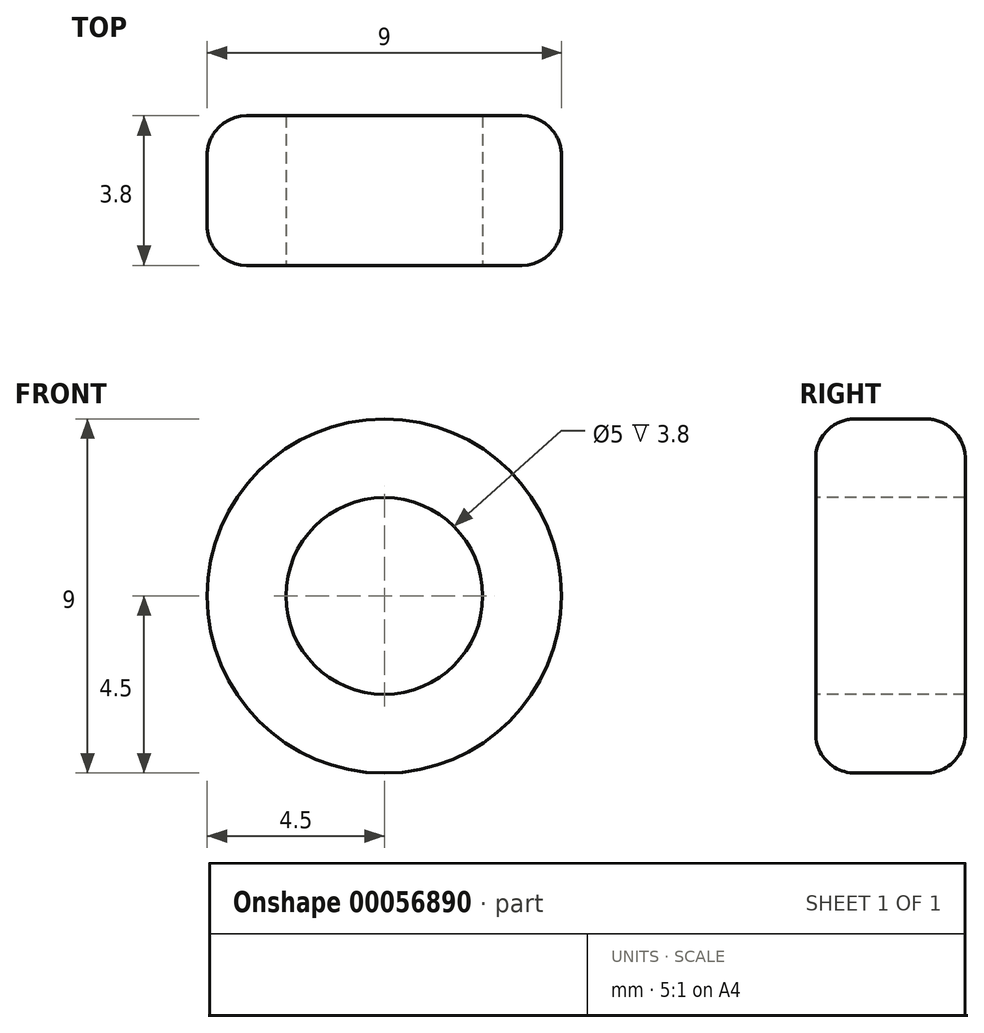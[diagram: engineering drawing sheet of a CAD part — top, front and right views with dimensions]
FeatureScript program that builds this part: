
annotation { "Feature Type Name" : "Feature", "Feature Type Description" : "" }
export const myFeature = defineFeature(function(context is Context, id is Id, definition is map)
    precondition{}
    {
        {
            var Q0;
            Q0=qCreatedBy(makeId("Right.planeOp"),FACE);
            var sketch = newSketch(context, id + "F0", { "sketchPlane" : qUnion([Q0])});
            skLineSegment(sketch, "E0", {"start": v(-1.95, 0.45) * mm, "end": v(-1.95, -0.55) * mm});
            skLineSegment(sketch, "E1", {"start": v(-1.95, -0.55) * mm, "end": v(1.85, -0.55) * mm});
            skLineSegment(sketch, "E2", {"start": v(1.85, 0.45) * mm, "end": v(1.85, -0.55) * mm});
            skLineSegment(sketch, "E3", {"start": v(-0.95, 1.45) * mm, "end": v(0.85, 1.45) * mm});
            skPoint(sketch, "E3.startSnap0", {"position": v(0, 1.45) * mm});
            skPoint(sketch, "E4.orphan", {"position": v(-1.95, 0) * mm});
            skPoint(sketch, "E5.start.orphan", {"position": v(1.85, 0) * mm});
            skArc(sketch, "E6.filletArc", {"start": v(1.85, 0.45) * mm, "mid": v(1.56, 1.16) * mm, "end": v(0.85, 1.45) * mm});
            skPoint(sketch, "E7.visualSharp", {"position": v(-1.95, 1.45) * mm});
            skArc(sketch, "E7.filletArc", {"start": v(-0.95, 1.45) * mm, "mid": v(-1.66, 1.16) * mm, "end": v(-1.95, 0.45) * mm});
            skSolve(sketch);
        }
        {
            var Q0;
            Q0=qCreatedBy(makeId("Right.planeOp"),FACE);
            var sketch = newSketch(context, id + "F1", { "sketchPlane" : qUnion([Q0])});
            skLineSegment(sketch, "E8", {"start": v(-3.91, -3.05) * mm, "end": v(4.29, -3.05) * mm});
            skSolve(sketch);
        }
        {
            var Q0;
            Q0=makeQuery(id+"F0.imprint","IMPRINT",FACE,{"disambiguationData":[TD([[makeQuery(id+"F0.imprint","IMPRINT",EDGE,{"derivedFrom":sQuery(id+"F0.wireOp",EDGE,"E5")}),1.0]])]});
            var Q1;
            Q1=makeQuery(id+"F0.imprint","IMPRINT",FACE,{"disambiguationData":[TD([[makeQuery(id+"F0.imprint","IMPRINT",EDGE,{"derivedFrom":sQuery(id+"F0.wireOp",EDGE,"E0")}),1.0]])]});
            var Q2;
            Q2=sQuery(id+"F1.wireOp",EDGE,"E8");
            revolve(context, id + "F2", {"entities" : qUnion([Q0, Q1]), "axis" : qUnion([Q2]), "revolveType" : RevolveType.FULL});
        }
    });
